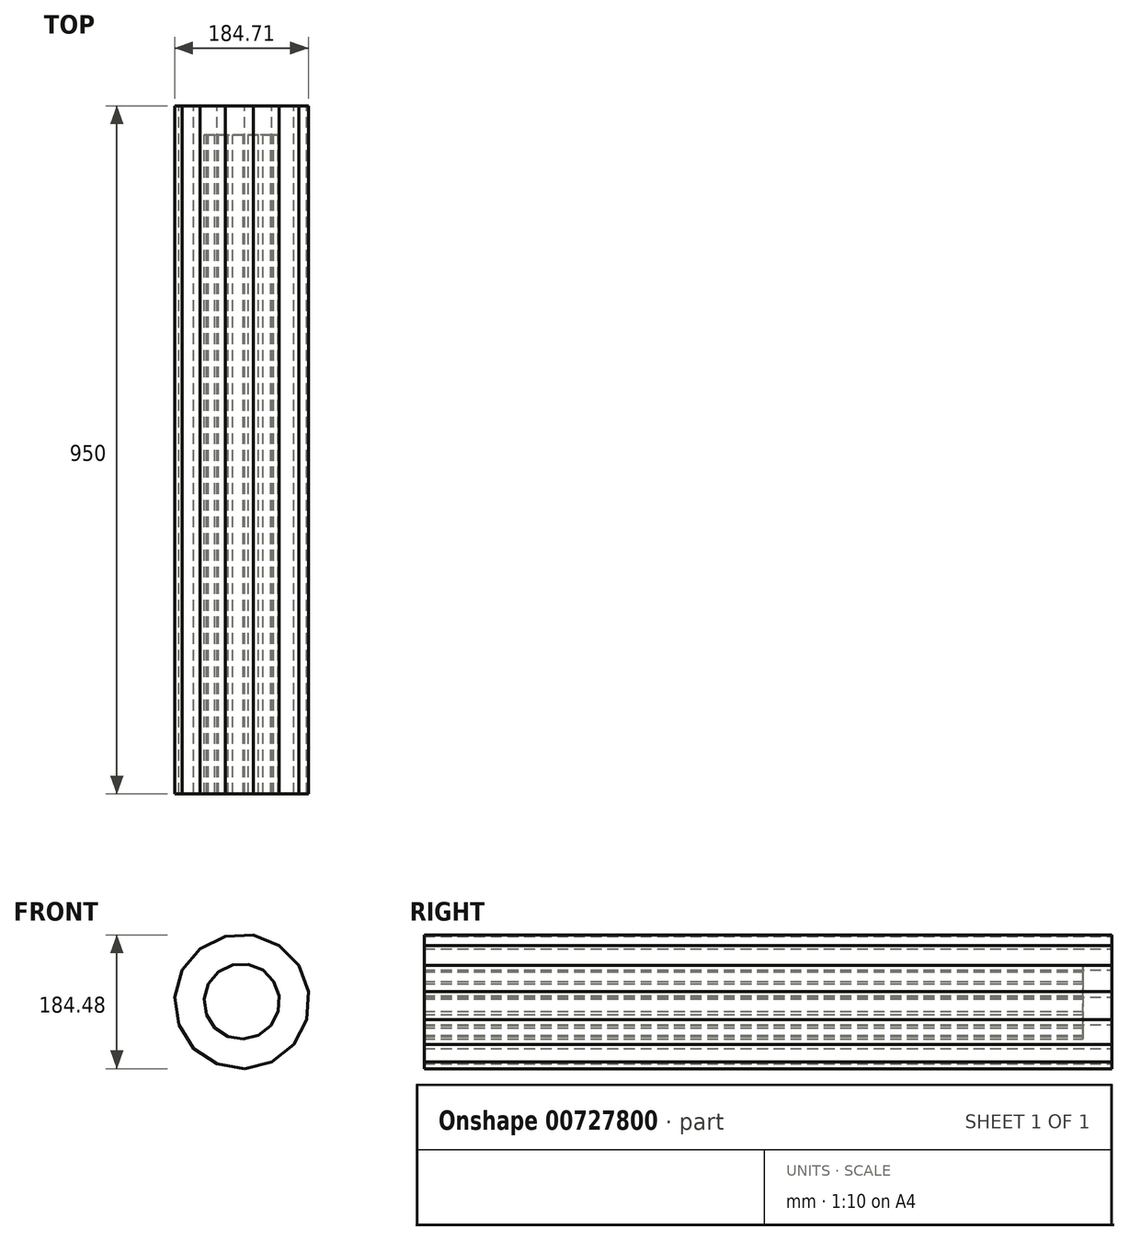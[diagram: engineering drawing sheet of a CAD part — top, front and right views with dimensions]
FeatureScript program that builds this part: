
annotation { "Feature Type Name" : "Feature", "Feature Type Description" : "" }
export const myFeature = defineFeature(function(context is Context, id is Id, definition is map)
    precondition{}
    {
        {
            var Q0;
            Q0=qCreatedBy(makeId("Front.planeOp"),FACE);
            var sketch = newSketch(context, id + "F0", { "sketchPlane" : qUnion([Q0])});
            skCircle(sketch, "E0.cCircle", {"center": v(0, 0) * mm, "radius": 90.9 * mm, "construction": true});
            skLineSegment(sketch, "E0.0", {"start": v(-66.47, -64.96) * mm, "end": v(-87.14, -32.31) * mm});
            skLineSegment(sketch, "E0.1", {"start": v(-87.14, -32.31) * mm, "end": v(-92.75, 5.93) * mm});
            skLineSegment(sketch, "E0.2", {"start": v(-92.75, 5.93) * mm, "end": v(-82.32, 43.14) * mm});
            skLineSegment(sketch, "E0.3", {"start": v(-82.32, 43.14) * mm, "end": v(-57.66, 72.9) * mm});
            skLineSegment(sketch, "E0.4", {"start": v(-57.66, 72.9) * mm, "end": v(-23.03, 90.04) * mm});
            skLineSegment(sketch, "E0.5", {"start": v(-23.03, 90.04) * mm, "end": v(15.59, 91.62) * mm});
            skLineSegment(sketch, "E0.6", {"start": v(15.59, 91.62) * mm, "end": v(51.5, 77.36) * mm});
            skLineSegment(sketch, "E0.7", {"start": v(51.5, 77.36) * mm, "end": v(78.52, 49.72) * mm});
            skLineSegment(sketch, "E0.8", {"start": v(78.52, 49.72) * mm, "end": v(91.96, 13.49) * mm});
            skLineSegment(sketch, "E0.9", {"start": v(91.96, 13.49) * mm, "end": v(89.5, -25.08) * mm});
            skLineSegment(sketch, "E0.10", {"start": v(89.5, -25.08) * mm, "end": v(71.55, -59.31) * mm});
            skLineSegment(sketch, "E0.11", {"start": v(71.55, -59.31) * mm, "end": v(41.24, -83.29) * mm});
            skLineSegment(sketch, "E0.12", {"start": v(41.24, -83.29) * mm, "end": v(3.8, -92.86) * mm});
            skLineSegment(sketch, "E0.13", {"start": v(3.8, -92.86) * mm, "end": v(-34.3, -86.38) * mm});
            skLineSegment(sketch, "E0.14", {"start": v(-34.3, -86.38) * mm, "end": v(-66.47, -64.96) * mm});
            skPoint(sketch, "E0.0.midPoint", {"position": v(-76.8, -48.64) * mm});
            skSolve(sketch);
        }
        {
            var Q0;
            Q0=makeQuery(id+"F0.imprint","IMPRINT",FACE,{"disambiguationData":[TD([[makeQuery(id+"F0.imprint","IMPRINT",EDGE,{"derivedFrom":sQuery(id+"F0.wireOp",EDGE,"E0.0")}),-1.0]])]});
            extrude(context, id + "F1", {"entities" : qUnion([Q0]), "depth" : 950 * mm, "offsetDistance" : 25.4 * mm});
        }
        {
            var Q0;
            Q0=makeQuery(id+"F1.opExtrude","CAP_FACE",FACE,{"disambiguationData":[OSD([sQuery(id+"F0.wireOp",EDGE,"E0.0"),sQuery(id+"F0.wireOp",EDGE,"E0.1"),sQuery(id+"F0.wireOp",EDGE,"E0.2"),sQuery(id+"F0.wireOp",EDGE,"E0.3"),sQuery(id+"F0.wireOp",EDGE,"E0.4"),sQuery(id+"F0.wireOp",EDGE,"E0.5"),sQuery(id+"F0.wireOp",EDGE,"E0.6"),sQuery(id+"F0.wireOp",EDGE,"E0.7"),sQuery(id+"F0.wireOp",EDGE,"E0.8"),sQuery(id+"F0.wireOp",EDGE,"E0.9"),sQuery(id+"F0.wireOp",EDGE,"E0.10"),sQuery(id+"F0.wireOp",EDGE,"E0.11"),sQuery(id+"F0.wireOp",EDGE,"E0.12"),sQuery(id+"F0.wireOp",EDGE,"E0.13"),sQuery(id+"F0.wireOp",EDGE,"E0.14")])],"isStart":false});
            shell(context, id + "F2", {"entities" : qUnion([Q0]), "thickness" : 40 * mm});
        }
    });
